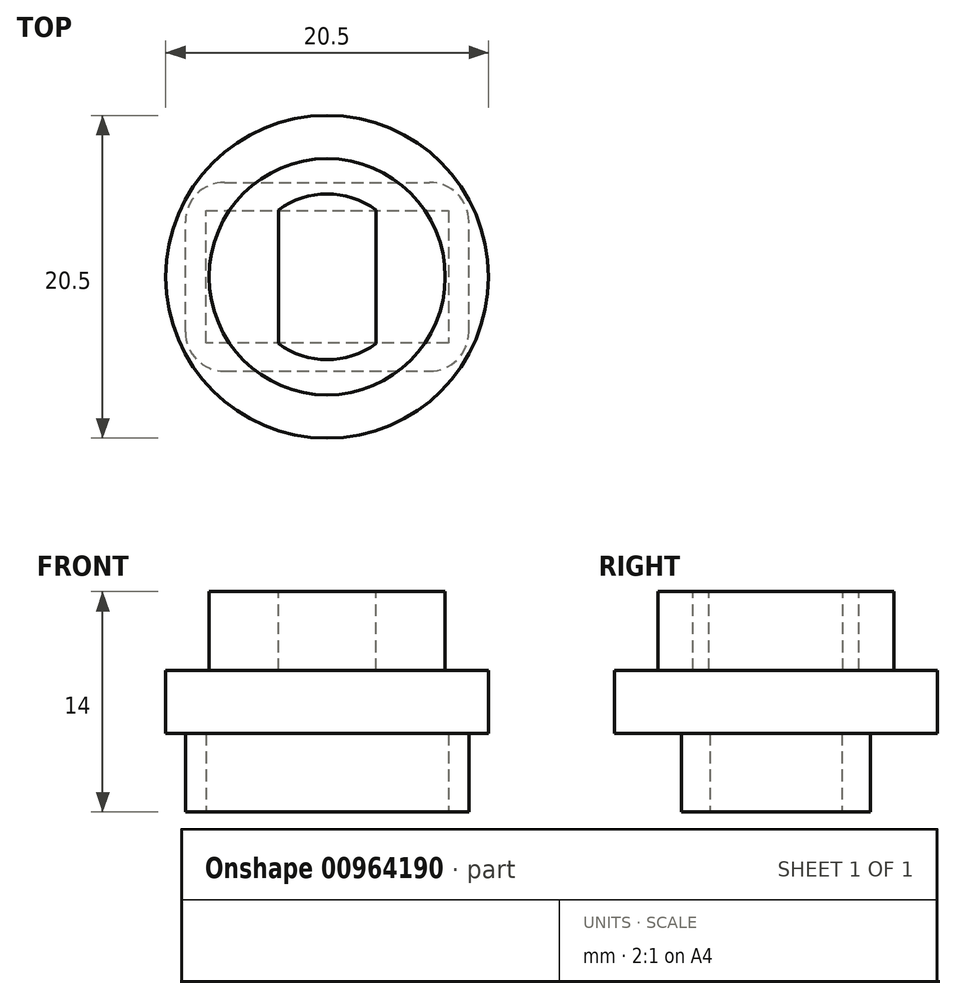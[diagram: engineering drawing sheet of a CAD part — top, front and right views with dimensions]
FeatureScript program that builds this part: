
annotation { "Feature Type Name" : "Feature", "Feature Type Description" : "" }
export const myFeature = defineFeature(function(context is Context, id is Id, definition is map)
    precondition{}
    {
        {
            var Q0;
            Q0=qCreatedBy(makeId("Top.planeOp"),FACE);
            var sketch = newSketch(context, id + "F0", { "sketchPlane" : qUnion([Q0])});
            skCircle(sketch, "E0", {"center": v(0, 0) * mm, "radius": 10.25 * mm});
            skSolve(sketch);
        }
        {
            var Q0;
            Q0 = qSketchRegion(id + "F0", true);
            extrude(context, id + "F1", {"entities" : qUnion([Q0]), "depth" : 4 * mm, "offsetDistance" : 25 * mm});
        }
        {
            var Q0;
            Q0=makeQuery(id+"F1.opExtrude","CAP_FACE",FACE,{"disambiguationData":[OSD([sQuery(id+"F0.wireOp",EDGE,"E0")])],"isStart":true});
            var sketch = newSketch(context, id + "F2", { "sketchPlane" : qUnion([Q0])});
            skLineSegment(sketch, "E1.bottom", {"start": v(-9, 6) * mm, "end": v(9, 6) * mm});
            skLineSegment(sketch, "E1.top", {"start": v(-9, -6) * mm, "end": v(9, -6) * mm});
            skLineSegment(sketch, "E1.left", {"start": v(-9, 6) * mm, "end": v(-9, -6) * mm});
            skLineSegment(sketch, "E1.right", {"start": v(9, 6) * mm, "end": v(9, -6) * mm});
            skSolve(sketch);
        }
        {
            var Q0;
            Q0 = qSketchRegion(id + "F2", true);
            extrude(context, id + "F3", {"entities" : qUnion([Q0]), "operationType" : NewBodyOperationType.ADD, "depth" : 5 * mm, "offsetDistance" : 25 * mm});
        }
        {
            var Q0;
            Q0=makeQuery(id+"F3.opExtrude","CAP_FACE",FACE,{"disambiguationData":[OSD([sQuery(id+"F2.wireOp",EDGE,"E1.bottom"),sQuery(id+"F2.wireOp",EDGE,"E1.top"),sQuery(id+"F2.wireOp",EDGE,"E1.left"),sQuery(id+"F2.wireOp",EDGE,"E1.right")])],"isStart":false});
            var sketch = newSketch(context, id + "F4", { "sketchPlane" : qUnion([Q0])});
            skLineSegment(sketch, "E2.0", {"start": v(-7.7, 4.2) * mm, "end": v(-7.7, -4.2) * mm});
            skLineSegment(sketch, "E2.1", {"start": v(7.7, 4.2) * mm, "end": v(-7.7, 4.2) * mm});
            skLineSegment(sketch, "E2.2", {"start": v(7.7, -4.2) * mm, "end": v(7.7, 4.2) * mm});
            skLineSegment(sketch, "E2.3", {"start": v(-7.7, -4.2) * mm, "end": v(7.7, -4.2) * mm});
            skSolve(sketch);
        }
        {
            var Q0;
            Q0 = qSketchRegion(id + "F4", true);
            extrude(context, id + "F5", {"entities" : qUnion([Q0]), "operationType" : NewBodyOperationType.REMOVE, "oppositeDirection" : true, "depth" : 5 * mm, "offsetDistance" : 25 * mm});
        }
        {
            var Q0;
            Q0=makeQuery(id+"F1.opExtrude","CAP_FACE",FACE,{"disambiguationData":[OSD([sQuery(id+"F0.wireOp",EDGE,"E0")])],"isStart":false});
            var sketch = newSketch(context, id + "F6", { "sketchPlane" : qUnion([Q0])});
            skCircle(sketch, "E3", {"center": v(0, 0) * mm, "radius": 7.5 * mm});
            skSolve(sketch);
        }
        {
            var Q0;
            Q0 = qSketchRegion(id + "F6", true);
            extrude(context, id + "F7", {"entities" : qUnion([Q0]), "operationType" : NewBodyOperationType.ADD, "depth" : 5 * mm, "offsetDistance" : 25 * mm});
        }
        {
            var Q0;
            Q0=makeQuery(id+"F7.opExtrude","CAP_FACE",FACE,{"disambiguationData":[OSD([sQuery(id+"F6.wireOp",EDGE,"E3")])],"isStart":false});
            var sketch = newSketch(context, id + "F8", { "sketchPlane" : qUnion([Q0])});
            skLineSegment(sketch, "E4.left", {"start": v(-3.1, 4.25) * mm, "end": v(-3.1, -4.25) * mm});
            skLineSegment(sketch, "E4.right", {"start": v(3.1, 4.25) * mm, "end": v(3.1, -4.25) * mm});
            skArc(sketch, "E5", {"start": v(3.1, 4.25) * mm, "mid": v(0, 5.26) * mm, "end": v(-3.1, 4.25) * mm});
            skArc(sketch, "E6", {"start": v(-3.1, -4.25) * mm, "mid": v(0, -5.26) * mm, "end": v(3.1, -4.25) * mm});
            skLineSegment(sketch, "E7", {"start": v(-3.1, 4.25) * mm, "end": v(3.1, 4.25) * mm, "construction": true});
            skLineSegment(sketch, "E8", {"start": v(-3.1, -4.25) * mm, "end": v(3.1, -4.25) * mm, "construction": true});
            skSolve(sketch);
        }
        {
            var Q0;
            Q0 = qSketchRegion(id + "F8", true);
            extrude(context, id + "F9", {"entities" : qUnion([Q0]), "operationType" : NewBodyOperationType.REMOVE, "oppositeDirection" : true, "depth" : 5 * mm, "offsetDistance" : 25 * mm});
        }
        {
            var Q0;
            Q0=makeQuery(id+"F3.opExtrude","SWEPT_EDGE",EDGE,{"disambiguationData":[OSD([sQuery(id+"F2.wireOp",EDGE,"E1.top"),sQuery(id+"F2.wireOp",EDGE,"E1.left")])]});
            var Q1;
            Q1=makeQuery(id+"F3.opExtrude","SWEPT_EDGE",EDGE,{"disambiguationData":[OSD([sQuery(id+"F2.wireOp",EDGE,"E1.bottom"),sQuery(id+"F2.wireOp",EDGE,"E1.left")])]});
            var Q2;
            Q2=makeQuery(id+"F3.opExtrude","SWEPT_EDGE",EDGE,{"disambiguationData":[OSD([sQuery(id+"F2.wireOp",EDGE,"E1.bottom"),sQuery(id+"F2.wireOp",EDGE,"E1.right")])]});
            var Q3;
            Q3=makeQuery(id+"F3.opExtrude","SWEPT_EDGE",EDGE,{"disambiguationData":[OSD([sQuery(id+"F2.wireOp",EDGE,"E1.top"),sQuery(id+"F2.wireOp",EDGE,"E1.right")])]});
            fillet(context, id + "F10", {"entities" : qUnion([Q0, Q1, Q2, Q3]), "radius" : 2.5 * mm, "tangentPropagation" : true, "allowEdgeOverflow" : false});
        }
    });
